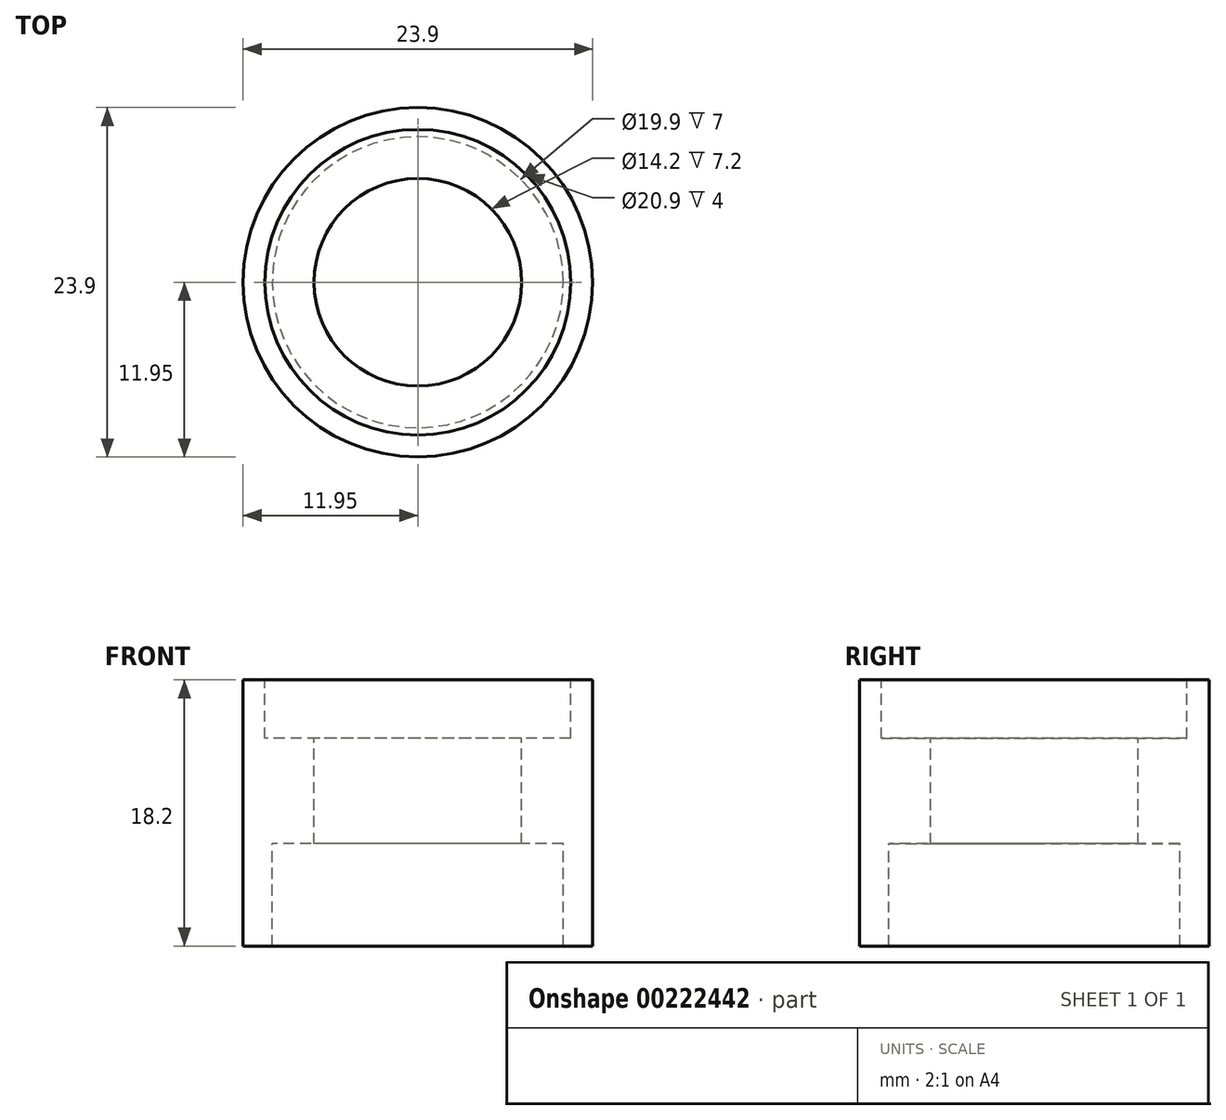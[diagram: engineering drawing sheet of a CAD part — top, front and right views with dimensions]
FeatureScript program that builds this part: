
annotation { "Feature Type Name" : "Feature", "Feature Type Description" : "" }
export const myFeature = defineFeature(function(context is Context, id is Id, definition is map)
    precondition{}
    {
        {
            var Q0;
            Q0=qCreatedBy(makeId("Front.planeOp"),FACE);
            var sketch = newSketch(context, id + "F0", { "sketchPlane" : qUnion([Q0])});
            skLineSegment(sketch, "E0", {"start": v(0, 51.04) * mm, "end": v(0, -46.39) * mm, "construction": true});
            skLineSegment(sketch, "E1", {"start": v(-9.95, 0) * mm, "end": v(-9.95, 7) * mm});
            skLineSegment(sketch, "E2", {"start": v(-9.95, 7) * mm, "end": v(-7.1, 7) * mm});
            skLineSegment(sketch, "E3", {"start": v(-11.95, 18.2) * mm, "end": v(-11.95, 0) * mm});
            skLineSegment(sketch, "E4", {"start": v(-11.95, 0) * mm, "end": v(-9.95, 0) * mm});
            skLineSegment(sketch, "E5", {"start": v(-11.95, 18.2) * mm, "end": v(-10.45, 18.2) * mm});
            skLineSegment(sketch, "E6", {"start": v(-10.45, 18.2) * mm, "end": v(-10.45, 14.2) * mm});
            skLineSegment(sketch, "E7", {"start": v(-10.45, 14.2) * mm, "end": v(-7.1, 14.2) * mm});
            skLineSegment(sketch, "E8", {"start": v(-7.1, 14.2) * mm, "end": v(-7.1, 7) * mm});
            skSolve(sketch);
        }
        {
            var Q0;
            Q0 = qSketchRegion(id + "F0", true);
            var Q1;
            Q1=sQuery(id+"F0.wireOp",EDGE,"E0");
            revolve(context, id + "F1", {"entities" : qUnion([Q0]), "axis" : qUnion([Q1]), "revolveType" : RevolveType.FULL});
        }
    });
